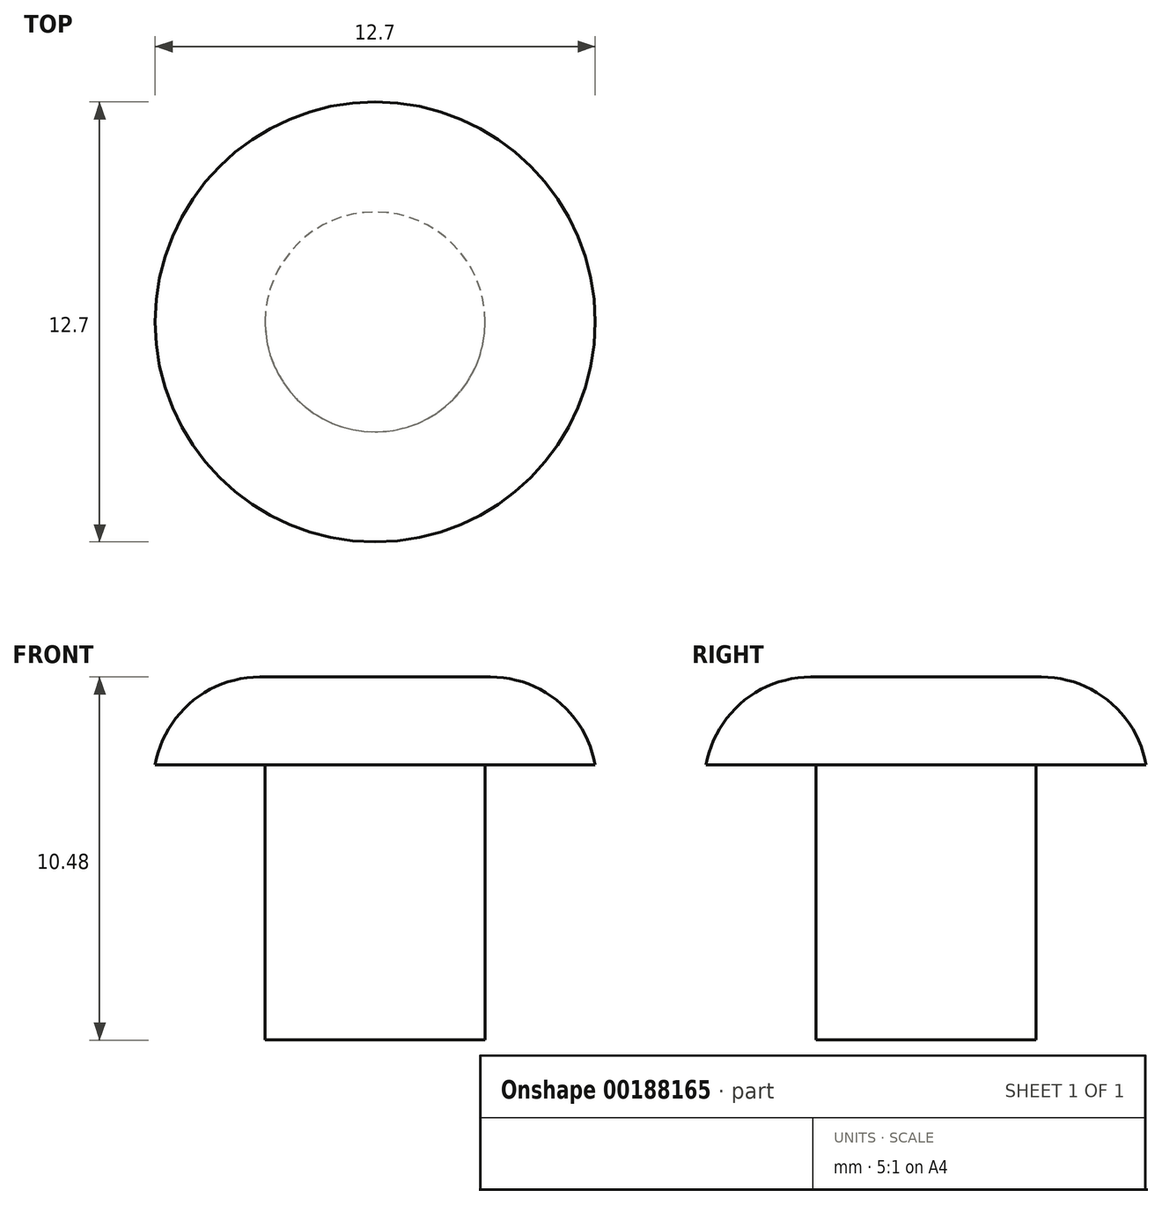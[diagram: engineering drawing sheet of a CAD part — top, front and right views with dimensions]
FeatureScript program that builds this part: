
annotation { "Feature Type Name" : "Feature", "Feature Type Description" : "" }
export const myFeature = defineFeature(function(context is Context, id is Id, definition is map)
    precondition{}
    {
        {
            var Q0;
            Q0=qCreatedBy(makeId("Top.planeOp"),FACE);
            var sketch = newSketch(context, id + "F0", { "sketchPlane" : qUnion([Q0])});
            skCircle(sketch, "E0", {"center": v(0, 0) * mm, "radius": 6.35 * mm});
            skSolve(sketch);
        }
        {
            var Q0;
            Q0 = qSketchRegion(id + "F0", true);
            extrude(context, id + "F1", {"entities" : qUnion([Q0]), "depth" : 2.54 * mm});
        }
        {
            var Q0;
            Q0=makeQuery(id+"F1.opExtrude","CAP_EDGE",EDGE,{"disambiguationData":[OSD([sQuery(id+"F0.wireOp",EDGE,"E0")])],"isStart":false});
            fillet(context, id + "F2", {"entities" : qUnion([Q0]), "radius" : 3.07 * mm, "tangentPropagation" : true, "allowEdgeOverflow" : false});
        }
        {
            var Q0;
            Q0=makeQuery(id+"F1.opExtrude","CAP_FACE",FACE,{"disambiguationData":[OSD([sQuery(id+"F0.wireOp",EDGE,"E0")])],"isStart":true});
            var sketch = newSketch(context, id + "F3", { "sketchPlane" : qUnion([Q0])});
            skCircle(sketch, "E1", {"center": v(0, 0) * mm, "radius": 3.18 * mm});
            skSolve(sketch);
        }
        {
            var Q0;
            Q0 = qSketchRegion(id + "F3", true);
            extrude(context, id + "F4", {"entities" : qUnion([Q0]), "operationType" : NewBodyOperationType.ADD, "depth" : 7.94 * mm});
        }
    });
